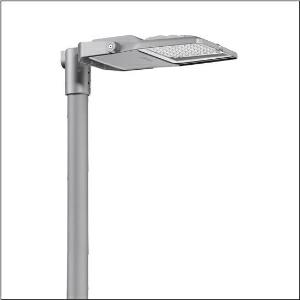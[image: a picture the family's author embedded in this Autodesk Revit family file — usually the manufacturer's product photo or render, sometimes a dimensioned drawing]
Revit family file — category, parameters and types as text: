
# Revit family: floodlight_fl_21_iq_mini___pl64_5xa7772c4e3a_b66a
name_source: partatom
category: Lighting Fixtures
units: mm (PartAtom-declared; Revit-internal decimal feet)

## family parameters
Cut with Voids When Loaded = No
Host = Face
Light Source = No
Part Type = Normal
Room Calculation Point = No
Round Connector Dimension = Use Diameter
Shared = No

## types (1)
- --- (1 x LED, 12280 lm, 87.2 W, 4000K)
    Apparent Load = 87 VA
    CIE Flux Codes = 28 80 98 100 100
    Color Rendering = 70
    Color Temperature = 4000K
    Default Elevation = 1800 mm
    Description = Floodlight FL 21 iQ mini, floodlight, primary light control with lens, of PMMA, primary optical cover: protective disc, of toughened safety glass, transparent, light distribution: PL64, light emission: direct distribution, installation type: surface-mounted, LED, High Power LED, rated luminous flux: 12.280lm, luminous efficacy: 141lm/W, light colour: 740, colour temperature: 4000K, control: Auto-Match, Temp-Guard, Night-Set, Smart-Wire, Desk-Remote (wireless, voltage-free reading and setting of iQ features in the workshop via application-optimized NFC function/RFID function), optimised constant luminous flux control (CLO 2.0), Light-Fading, Lumen-Switch, with terminal, 6-pole, mains connection: 220..240V, AC, 50/60Hz, start of lifetime: 87W, end of service life: 92W, reduction: 40W, luminaire housing, of diecast aluminium, powder-coated, Siteco® metallic grey (DB 702S), corrosivity category C5 mid according to DIN EN ISO 12944, sealing non-destructively replaceable, please order mast flange separately, mast bracket, of steel, galvanised, powder-coated, protection rating (complete): IP66, insulation class (complete): insulation class II (safety insulation), certification: CE, ENEC, VDE, protection symbol: D, impact resistance: IK08, permissible operating ambient temperature: -40..+40°C, permissible operating ambient temperature for outdoor applications: -40..+50°C, standard: DIN EN 12944, LABS conformity tested according to VDMA 24364:2018-05, packaging unit: 1 piece

Light Distribution: PL64
    Height = 70 mm
    Lamp = 1 x LED
    Lamp Light Flux = 12280 lm
    Lamp Power = 87.2 W
    Lamp count = 1
    Length = 485 mm
    Luminous efficacy = 141 lm/W
    Manufacturer = Siteco
    ModVariant = No
    Model = 5XA7772C4E3A
    Number of Poles = 1
    OnlyDefault = Yes
    Power Factor = 1
    Product Name = Floodlight FL 21 iQ mini | PL64
    Product group = floodlight | pylon annexe
    ProductGroupID = 6200
    Protection Class = Protection class II
    Protection Degree = IP 66
    RLX_Detail_Level = 1
    RLX_Emergency_Light_Flux = 0 lm
    RLX_Emergency_Type = 0
    RLX_Emergency_Type_DB = No
    RlxData = <blob elided: 101285 chars, md5=31df178e>
    Socket = socket
    Standby Power = 0 W
    System Light Flux = 12280 lm
    System Power = 87 W
    Type Comments = factory setting: luminous flux: 100 % | dim-lin: 254 | 456 mA
    Type Image = l_1007125.jpg
    URL = http://relux.com
    VarID = @adj_116369
    Voltage = 0 V
    Weight = 0.00 kg
    Width = 337 mm

## geometry (parser evidence)
native form markers: Blend x4, Sweep x12
no freeform markers — native parametric forms only
